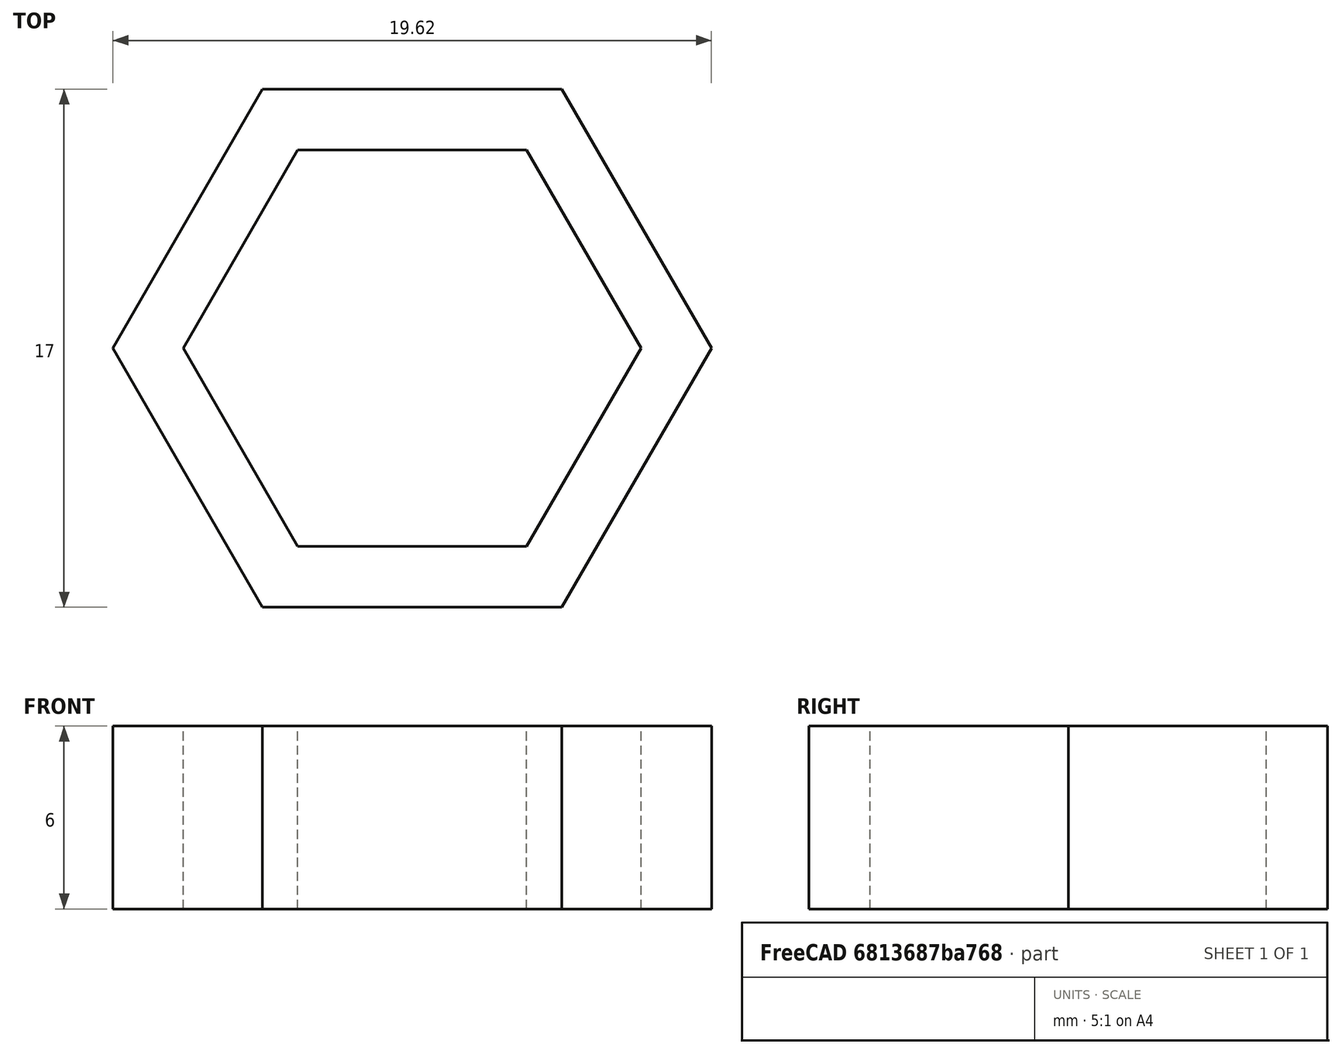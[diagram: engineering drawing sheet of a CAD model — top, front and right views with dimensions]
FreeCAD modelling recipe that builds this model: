
FCSTD DOCUMENT  (FreeCAD 0.20R29603 (Git))
Label: porca
License: All rights reserved
LicenseURL: http://en.wikipedia.org/wiki/All_rights_reserved
objects: Sketcher::SketchObject×1, PartDesign::Pad×1, PartDesign::Body×1
note: 4 computed .brp shape members not serialized (recipe doc carries the construction recipe); baked Part::Feature solids carry a one-line shape summary decoded from their .brp

FEATURE [Sketcher::SketchObject] Sketch
  FullyConstrained = true
  MapMode = 5
  Support = -> [XY_Plane]
  sketch-geometry (14):
    g0: LineSegment StartX=9.81495 StartY=0 StartZ=0 EndX=4.90748 EndY=8.5 EndZ=0
    g1: LineSegment StartX=4.90748 StartY=8.5 StartZ=0 EndX=-4.90748 EndY=8.5 EndZ=0
    g2: LineSegment StartX=-4.90748 StartY=8.5 StartZ=0 EndX=-9.81495 EndY=1.8e-15 EndZ=0
    g3: LineSegment StartX=-9.81495 StartY=1e-15 StartZ=0 EndX=-4.90748 EndY=-8.5 EndZ=0
    g4: LineSegment StartX=-4.90748 StartY=-8.5 StartZ=0 EndX=4.90748 EndY=-8.5 EndZ=0
    g5: LineSegment StartX=4.90748 StartY=-8.5 StartZ=0 EndX=9.81495 EndY=0 EndZ=0
    g6: Circle CenterX=0 CenterY=0 CenterZ=0 NormalX=0 NormalY=0 NormalZ=1 AngleXU=0 Radius=9.81495
    g7: LineSegment StartX=7.50555 StartY=0 StartZ=0 EndX=3.75278 EndY=6.5 EndZ=0
    g8: LineSegment StartX=3.75278 StartY=6.5 StartZ=0 EndX=-3.75278 EndY=6.5 EndZ=0
    g9: LineSegment StartX=-3.75278 StartY=6.5 StartZ=0 EndX=-7.50555 EndY=0 EndZ=0
    g10: LineSegment StartX=-7.50555 StartY=0 StartZ=0 EndX=-3.75278 EndY=-6.5 EndZ=0
    g11: LineSegment StartX=-3.75278 StartY=-6.5 StartZ=0 EndX=3.75278 EndY=-6.5 EndZ=0
    g12: LineSegment StartX=3.75278 StartY=-6.5 StartZ=0 EndX=7.50555 EndY=0 EndZ=0
    g13: Circle CenterX=0 CenterY=0 CenterZ=0 NormalX=0 NormalY=0 NormalZ=1 AngleXU=0 Radius=7.50555
  constraints (32):
    c: Coincident(g0,g1)
    c: Coincident(g1,g2)
    c: Coincident(g2,g3)
    c: Coincident(g3,g4)
    c: Coincident(g4,g5)
    c: Coincident(g5,g0)
    c: Equal(g0, g1-g5) x5
    c: PointOnObject(g0,g6)
    c: PointOnObject(g1,g6)
    c: PointOnObject(g2,g6)
    c: PointOnObject(g3,g6)
    c: PointOnObject(g4,g6)
    c: PointOnObject(g5,g6)
    c: Coincident(g6,g-1)
    c: PointOnObject(g5,g-1)
    c: Coincident(g7,g8)
    c: Coincident(g8,g9)
    c: Coincident(g9,g10)
    c: Coincident(g10,g11)
    c: Coincident(g11,g12)
    c: Coincident(g12,g7)
    c: Equal(g7, g8-g12) x5
    c: PointOnObject(g7,g13)
    c: PointOnObject(g8,g13)
    c: PointOnObject(g9,g13)
    c: PointOnObject(g10,g13)
    c: PointOnObject(g11,g13)
    c: PointOnObject(g12,g13)
    c: Coincident(g13,g6)
    c: PointOnObject(g12,g-1)
    c: Distance(g1,g3) = 17
    c: DistanceY(g10,g8) = 13
FEATURE [PartDesign::Pad] Pad
  Direction = (0,0,1)
  Length = 6
  Length2 = 10
  Profile = -> Sketch
  ReferenceAxis = -> Sketch [N_Axis]
  Type = 0
FEATURE [PartDesign::Body] Body
  Group = -> [Sketch,Pad]
  Origin = -> Origin
  Tip = -> Pad
